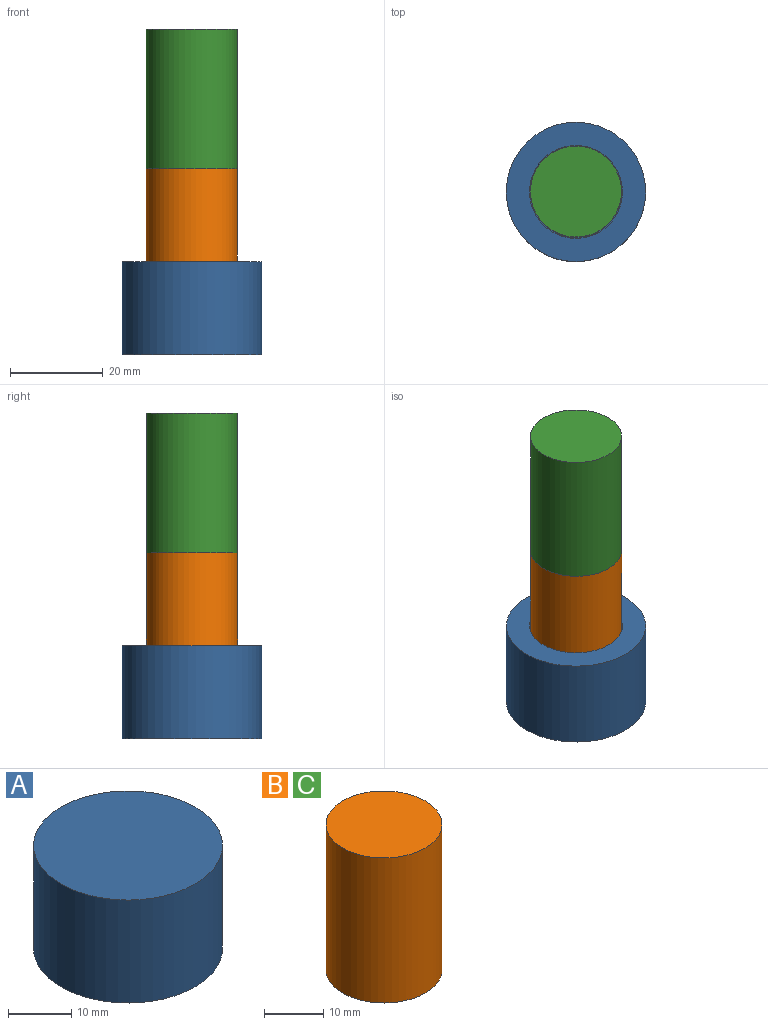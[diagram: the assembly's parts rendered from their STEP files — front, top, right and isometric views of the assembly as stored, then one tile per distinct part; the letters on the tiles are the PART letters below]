
ASSEMBLY  parts=3 mates=2
PART A: 5 faces, bbox 30x30x20 mm
  f0: cylinder r=15mm len=30mm, axis (0,0,-1), area 1885mm2, adj f1,f2
  f1: plane 30x30mm, normal (0,0,1), area 706.9mm2, adj f0
  f2: plane 30x30mm, normal (0,0,-1), area 392.7mm2, adj f0,f3
  f3: cylinder r=10mm len=20mm, axis (0,0,-1), area 942.5mm2, adj f2,f4
  f4: plane 20x20mm, normal (0,0,-1), area 314.2mm2, adj f3
PART B: 3 faces, bbox 19.6x19.6x30 mm
  f0: cylinder r=9.8mm len=30mm, axis (0,0,-1), area 1847.3mm2, adj f1,f2
  f1: plane 19.6x19.6mm, normal (0,0,1), area 301.7mm2, adj f0
  f2: plane 19.6x19.6mm, normal (0,0,-1), area 301.7mm2, adj f0
PART C: same geometry as B
PLACE A rot(axis=(-1,0,0),180deg) t=(-29.38,78.48,3.19)mm
PLACE B rot(axis=(0.23,-0.25,0.94),0deg) t=(-22.22,54.01,-6.81)mm
PLACE C rot(axis=(0.23,-0.25,0.94),0deg) t=(-22.22,54.01,23.19)mm
MATE slider B.f0 <-> A.f0  axis (0,0,-1) through (-52.13,46.44,-6.81)mm
MATE fastened C.f0 <-> B.f0  axis (0,0,-1) through (-52.13,46.44,23.19)mm
